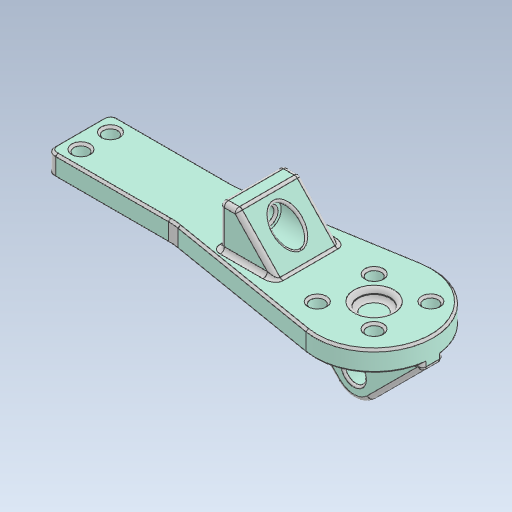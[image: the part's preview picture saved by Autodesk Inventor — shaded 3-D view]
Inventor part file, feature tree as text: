
AUTODESK INVENTOR PART (.ipt)
format: ipt  version: 2021.2 (Build 252289000, 289)  size: 713,216 bytes
history: native  units: mm
features: fillet x8, other x4, chamfer x2
ambient origin geometry x8: Origin, YZ Plane, XZ Plane, XY Plane, X Axis, Y Axis, Z Axis, Center Point
bodies: Body1 (feature_tree)
feature tree (14):
  other  "Твёрдое тело.ipt"
  fillet  "Сопряжение1"  Radius=10.0mm
  chamfer  "Фаска1"  Distance=2.0mm
  chamfer  "Фаска2"  Distance=0.5mm Angle=45.0deg
  fillet  "Сопряжение2"  Radius=0.5mm
  fillet  "Сопряжение3"  Radius=1.0mm
  fillet  "Сопряжение9"  Radius=1.0mm
  fillet  "Сопряжение5"  Radius=1.0mm
  fillet  "Сопряжение6"  Radius=0.5mm
  fillet  "Сопряжение7"  Radius=1.0mm
  fillet  "Сопряжение8"  Radius=0.5mm
  other  "Ложечка::Твёрдое тело.ipt"
  other  "Элемент создания тегов1"
  other  "Твердое тело1"
